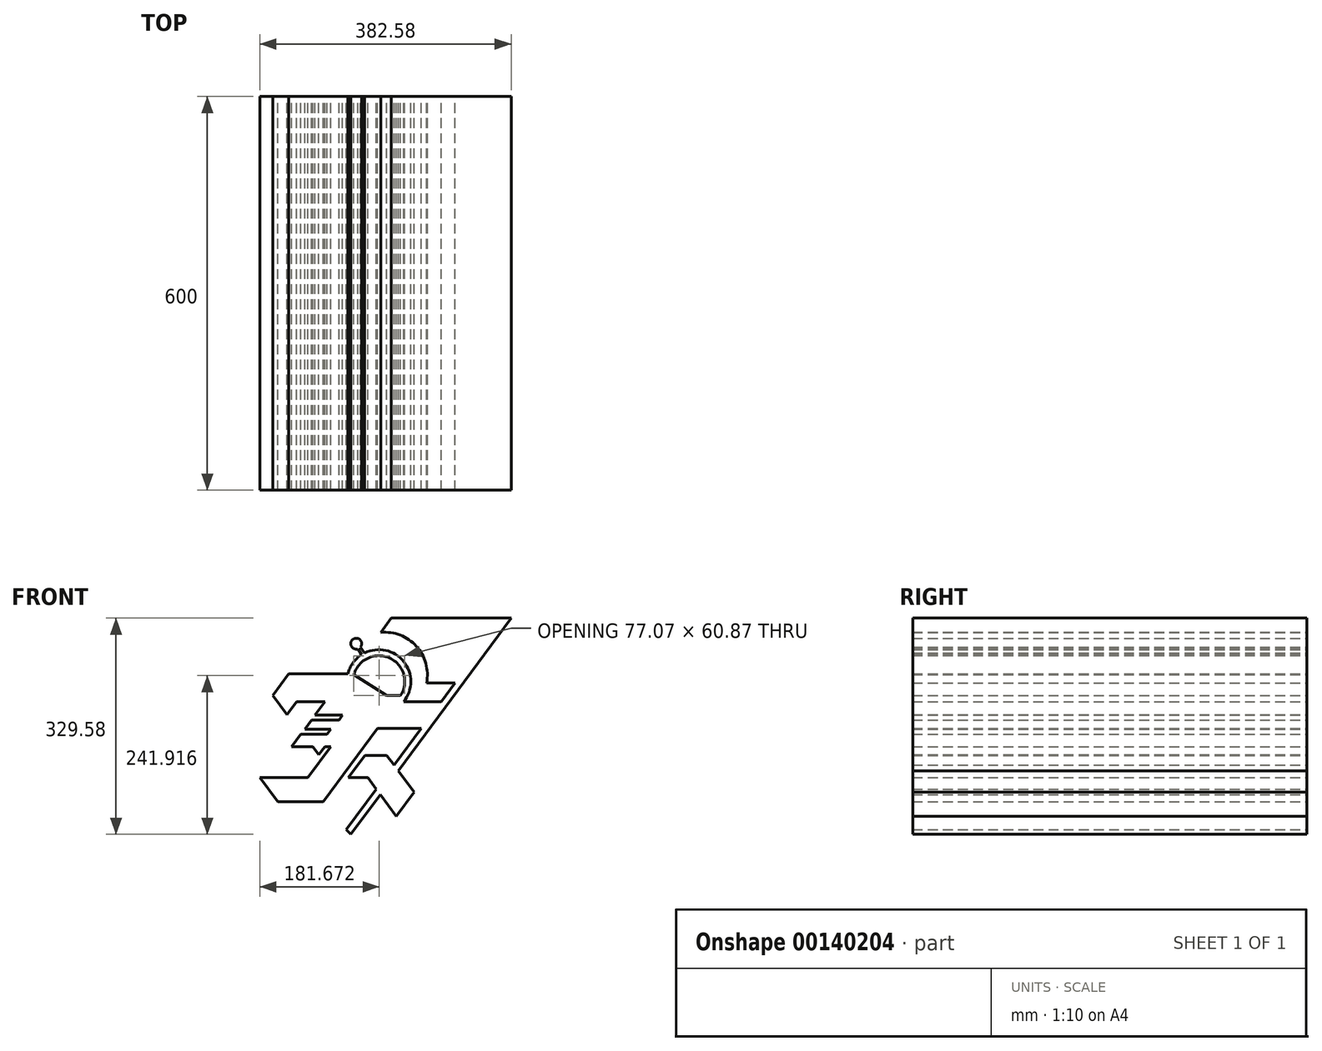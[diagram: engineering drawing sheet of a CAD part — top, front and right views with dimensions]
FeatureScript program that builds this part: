
annotation { "Feature Type Name" : "Feature", "Feature Type Description" : "" }
export const myFeature = defineFeature(function(context is Context, id is Id, definition is map)
    precondition{}
    {
        {
            var Q0;
            Q0=qCreatedBy(makeId("Front.planeOp"),FACE);
            var sketch = newSketch(context, id + "F0", { "sketchPlane" : qUnion([Q0])});
            skLineSegment(sketch, "E0.bottom", {"start": v(-135, 0) * mm, "end": v(0, 0) * mm});
            skLineSegment(sketch, "E0.top", {"start": v(-165.34, -41) * mm, "end": v(-30.34, -41) * mm});
            skLineSegment(sketch, "E0.left", {"start": v(-135, 0) * mm, "end": v(-165.34, -41) * mm});
            skLineSegment(sketch, "E0.right", {"start": v(0, 0) * mm, "end": v(-30.34, -41) * mm});
            skLineSegment(sketch, "E1", {"start": v(-30.34, -41) * mm, "end": v(-144.54, -195.34) * mm});
            skLineSegment(sketch, "E2", {"start": v(0, 0) * mm, "end": v(94.15, 127.23) * mm});
            skLineSegment(sketch, "E3", {"start": v(94.15, 127.23) * mm, "end": v(106.59, 127.23) * mm});
            skLineSegment(sketch, "E4", {"start": v(106.59, 127.23) * mm, "end": v(-137.29, -202.35) * mm});
            skLineSegment(sketch, "E5", {"start": v(-137.29, -202.35) * mm, "end": v(-144.54, -195.34) * mm});
            skLineSegment(sketch, "E6", {"start": v(94.15, 127.23) * mm, "end": v(-75.73, 127.23) * mm});
            skLineSegment(sketch, "E7", {"start": v(-75.73, 127.23) * mm, "end": v(-148.9, 28.36) * mm, "construction": true});
            skLineSegment(sketch, "E8", {"start": v(-22.25, 28.36) * mm, "end": v(20.99, 28.36) * mm});
            skArc(sketch, "E9", {"start": v(-22.25, 28.36) * mm, "mid": v(-37.66, 84.43) * mm, "end": v(-91.89, 105.4) * mm});
            skPoint(sketch, "E9.first.point", {"position": v(-91.89, 105.4) * mm});
            skPoint(sketch, "E9.second.point", {"position": v(-22.25, 28.36) * mm});
            skPoint(sketch, "E9.third.point", {"position": v(-148.9, 28.36) * mm});
            skLineSegment(sketch, "E10", {"start": v(-91.89, 105.4) * mm, "end": v(-75.73, 127.23) * mm});
            skLineSegment(sketch, "E11", {"start": v(-116.22, -81.86) * mm, "end": v(-82.78, -81.86) * mm});
            skLineSegment(sketch, "E12", {"start": v(-82.78, -81.86) * mm, "end": v(-41.05, -138.25) * mm});
            skLineSegment(sketch, "E13", {"start": v(-41.05, -138.25) * mm, "end": v(-68.07, -174.78) * mm});
            skLineSegment(sketch, "E14", {"start": v(-68.07, -174.78) * mm, "end": v(-111.71, -115.8) * mm});
            skLineSegment(sketch, "E15", {"start": v(-111.71, -115.8) * mm, "end": v(-141.34, -115.8) * mm});
            skLineSegment(sketch, "E16", {"start": v(-141.34, -115.8) * mm, "end": v(-116.22, -81.86) * mm});
            skLineSegment(sketch, "E17", {"start": v(0, 0) * mm, "end": v(0, -384.66) * mm, "construction": true});
            skArc(sketch, "E18", {"start": v(-61.72, 9.13) * mm, "mid": v(-78.72, 66.57) * mm, "end": v(-132.85, 40.92) * mm});
            skPoint(sketch, "E18.first.point", {"position": v(-132.85, 40.92) * mm});
            skPoint(sketch, "E18.second.point", {"position": v(-61.72, 9.13) * mm});
            skPoint(sketch, "E18.third.point", {"position": v(-62.22, 52.77) * mm});
            skArc(sketch, "E19", {"start": v(-57.02, 0) * mm, "mid": v(-73.23, 74.13) * mm, "end": v(-142.03, 42.1) * mm});
            skLineSegment(sketch, "E20", {"start": v(-96.94, -41) * mm, "end": v(-179.57, -152.66) * mm});
            skLineSegment(sketch, "E21", {"start": v(-179.57, -152.66) * mm, "end": v(-248.71, -152.66) * mm});
            skLineSegment(sketch, "E22", {"start": v(-248.71, -152.66) * mm, "end": v(-275.99, -115.8) * mm});
            skLineSegment(sketch, "E23", {"start": v(-275.99, -115.8) * mm, "end": v(-202.94, -115.8) * mm});
            skLineSegment(sketch, "E24", {"start": v(-202.94, -115.8) * mm, "end": v(-168.02, -68.62) * mm});
            skLineSegment(sketch, "E25", {"start": v(-168.02, -68.62) * mm, "end": v(-227.77, -68.62) * mm});
            skLineSegment(sketch, "E26", {"start": v(-227.77, -68.62) * mm, "end": v(-213.92, -49.9) * mm});
            skLineSegment(sketch, "E27", {"start": v(-213.92, -49.9) * mm, "end": v(-173.67, -49.9) * mm});
            skLineSegment(sketch, "E28", {"start": v(-173.67, -49.9) * mm, "end": v(-167.8, -41.98) * mm});
            skLineSegment(sketch, "E29", {"start": v(-167.8, -41.98) * mm, "end": v(-207.49, -41.98) * mm});
            skLineSegment(sketch, "E30", {"start": v(-207.49, -41.98) * mm, "end": v(-197.06, -27.89) * mm});
            skLineSegment(sketch, "E31", {"start": v(-197.06, -27.89) * mm, "end": v(-155.63, -27.89) * mm});
            skLineSegment(sketch, "E32", {"start": v(-155.63, -27.89) * mm, "end": v(-150.17, -20.5) * mm});
            skLineSegment(sketch, "E33", {"start": v(-150.17, -20.5) * mm, "end": v(-191.88, -20.5) * mm});
            skLineSegment(sketch, "E34", {"start": v(-191.88, -20.5) * mm, "end": v(-176.71, 0) * mm});
            skLineSegment(sketch, "E35", {"start": v(-176.71, 0) * mm, "end": v(-220.3, 0) * mm});
            skLineSegment(sketch, "E36", {"start": v(-220.3, 0) * mm, "end": v(-235, -19.84) * mm});
            skLineSegment(sketch, "E37", {"start": v(-235, -19.84) * mm, "end": v(-256.44, 9.15) * mm});
            skLineSegment(sketch, "E38", {"start": v(-256.44, 9.15) * mm, "end": v(-232.06, 42.1) * mm});
            skLineSegment(sketch, "E39", {"start": v(-232.06, 42.1) * mm, "end": v(-142.03, 42.1) * mm});
            skLineSegment(sketch, "E40", {"start": v(-61.72, 9.13) * mm, "end": v(-82.85, 9.13) * mm});
            skLineSegment(sketch, "E41", {"start": v(-82.85, 9.13) * mm, "end": v(-132.85, 40.92) * mm});
            skCircle(sketch, "E42", {"center": v(-129.37, 88.29) * mm, "radius": 8.37 * mm});
            skPoint(sketch, "E42.first.point", {"position": v(-135.33, 94.15) * mm});
            skPoint(sketch, "E42.second.point", {"position": v(-121.06, 89.33) * mm});
            skPoint(sketch, "E42.third.point", {"position": v(-132.3, 80.45) * mm});
            skLineSegment(sketch, "E43", {"start": v(-126.92, 80.28) * mm, "end": v(-120.82, 71.64) * mm});
            skLineSegment(sketch, "E44", {"start": v(-122.84, 83.04) * mm, "end": v(-116.5, 74.07) * mm});
            skLineSegment(sketch, "E45", {"start": v(-195.4, -68.62) * mm, "end": v(-186.19, -80.7) * mm});
            skLineSegment(sketch, "E46", {"start": v(-186.19, -80.7) * mm, "end": v(-177.24, -68.62) * mm});
            skSolve(sketch);
        }
        {
            var Q0;
            Q0=makeQuery(id+"F0.imprint","IMPRINT",FACE,{"disambiguationData":[TD([[makeQuery(id+"F0.imprint","IMPRINT",EDGE,{"derivedFrom":sQuery(id+"F0.wireOp",EDGE,"E0.bottom")}),-1.0]])]});
            var Q1;
            Q1 = qSketchRegion(id + "F0", true);
            extrude(context, id + "F1", {"entities" : qUnion([Q0, Q1]), "depth" : 600 * mm});
        }
    });
